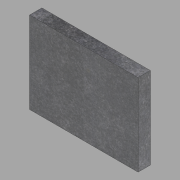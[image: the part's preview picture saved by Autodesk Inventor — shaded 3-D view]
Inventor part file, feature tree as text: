
AUTODESK INVENTOR PART (.ipt)
format: ipt  version: 2022.1 (Build 261234020, 234B)  size: 102,400 bytes
history: native  units: in
note: dims shown in document units (in); Inventor stores cm internally (conversion verified against a paired STEP export)
features: extrude x1, sketch x1
ambient origin geometry x8: Origin, YZ Plane, XZ Plane, XY Plane, X Axis, Y Axis, Z Axis, Center Point
bodies: Solid1 (feature_tree)
feature tree (2):
  extrude  "Extrusion1"  Depth=40.0in
  sketch  "Sketch1"  dims[d0=53.0in d1=40.0in d2=6.0in d3=0.0in]
